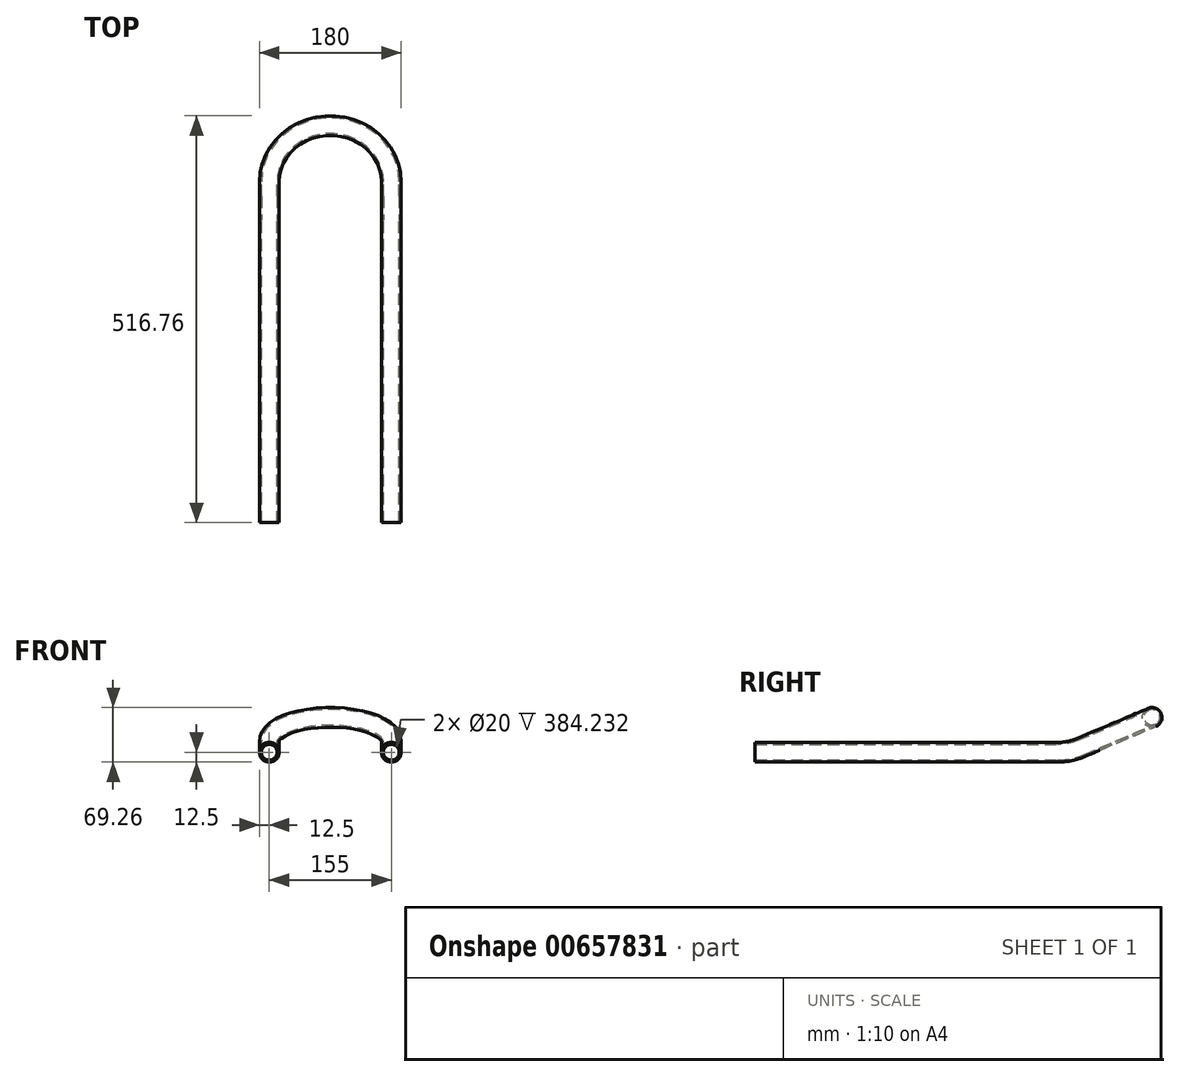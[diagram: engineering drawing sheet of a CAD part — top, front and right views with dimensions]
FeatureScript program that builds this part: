
annotation { "Feature Type Name" : "Feature", "Feature Type Description" : "" }
export const myFeature = defineFeature(function(context is Context, id is Id, definition is map)
    precondition{}
    {
        {
            var Q0;
            Q0=qCreatedBy(makeId("Top.planeOp"),FACE);
            var sketch = newSketch(context, id + "F0", { "sketchPlane" : qUnion([Q0])});
            skLineSegment(sketch, "E0", {"start": v(0, 0) * mm, "end": v(31.84, 0) * mm, "construction": true});
            skSolve(sketch);
        }
        {
            var Q0;
            Q0=qCreatedBy(makeId("Top.planeOp"),FACE);
            var Q1;
            Q1=sQuery(id+"F0.wireOp",EDGE,"E0");
            cPlane(context, id + "F1", {"entities" : qUnion([Q0, Q1]), "cplaneType" : CPlaneType.LINE_ANGLE, "offset" : 25.4 * mm, "angle" : 23 * degree, "width" : 152.4 * mm, "height" : 152.4 * mm});
        }
        {
            var Q0;
            Q0=qCreatedBy(makeId("Top.planeOp"),FACE);
            var sketch = newSketch(context, id + "F2", { "sketchPlane" : qUnion([Q0])});
            skLineSegment(sketch, "E1", {"start": v(77.5, 0) * mm, "end": v(77.5, -400) * mm});
            skSolve(sketch);
        }
        {
            var Q0;
            Q0=qCreatedBy(id+"F1.planeOp",FACE);
            var sketch = newSketch(context, id + "F3", { "sketchPlane" : qUnion([Q0])});
            skPoint(sketch, "E2.0", {"position": v(77.5, 0) * mm});
            skLineSegment(sketch, "E3", {"start": v(77.5, 0) * mm, "end": v(77.5, -35.77) * mm, "construction": true});
            skLineSegment(sketch, "E4", {"start": v(77.5, -35.77) * mm, "end": v(0, -35.77) * mm, "construction": true});
            skLineSegment(sketch, "E5", {"start": v(0, -35.77) * mm, "end": v(0, 0) * mm, "construction": true});
            skLineSegment(sketch, "E6", {"start": v(0, 0) * mm, "end": v(77.5, 0) * mm, "construction": true});
            skArc(sketch, "E7", {"start": v(77.5, -35.77) * mm, "mid": v(54.8, -90.57) * mm, "end": v(0, -113.27) * mm});
            skSolve(sketch);
        }
        {
            var Q0;
            Q0=sQuery(id+"F2.wireOp",VERTEX,"E1.end");
            var Q1;
            Q1=qCreatedBy(makeId("Front.planeOp"),FACE);
            cPlane(context, id + "F4", {"entities" : qUnion([Q0, Q1]), "cplaneType" : CPlaneType.PLANE_POINT, "offset" : 25 * mm, "width" : 150 * mm, "height" : 150 * mm});
        }
        {
            var Q0;
            Q0=qCreatedBy(id+"F4.planeOp",FACE);
            var sketch = newSketch(context, id + "F5", { "sketchPlane" : qUnion([Q0])});
            skPoint(sketch, "E8.0", {"position": v(77.5, 0) * mm});
            skCircle(sketch, "E9", {"center": v(77.5, 0) * mm, "radius": 12.5 * mm});
            skCircle(sketch, "E10.0", {"center": v(77.5, 0) * mm, "radius": 10 * mm});
            skSolve(sketch);
        }
        {
            var Q0;
            Q0=sQuery(id+"F2.wireOp",EDGE,"E1");
            var Q1;
            Q1=sQuery(id+"F3.wireOp",EDGE,"E3");
            cPlane(context, id + "F6", {"entities" : qUnion([Q0, Q1]), "cplaneType" : CPlaneType.LINE_ANGLE, "offset" : 25 * mm, "angle" : 0 * degree, "width" : 150 * mm, "height" : 150 * mm});
        }
        {
            var Q0;
            Q0=qCreatedBy(id+"F6.planeOp",FACE);
            var sketch = newSketch(context, id + "F7", { "sketchPlane" : qUnion([Q0])});
            skLineSegment(sketch, "E11.0", {"start": v(-14.51, 6.16) * mm, "end": v(-32.92, 13.98) * mm});
            skLineSegment(sketch, "E11.1", {"start": v(15.77, 0) * mm, "end": v(400, 0) * mm});
            skPoint(sketch, "E12.visualSharp", {"position": v(0, 0) * mm});
            skArc(sketch, "E12.filletArc", {"start": v(-14.51, 6.16) * mm, "mid": v(0.32, 1.56) * mm, "end": v(15.77, 0) * mm});
            skPoint(sketch, "E13", {"position": v(15.77, 0) * mm});
            skPoint(sketch, "E14", {"position": v(-14.51, 6.16) * mm});
            skSolve(sketch);
        }
        {
            var Q0;
            Q0=makeQuery(id+"F5.imprint","IMPRINT",FACE,{"disambiguationData":[TD([[makeQuery(id+"F5.imprint","IMPRINT",EDGE,{"derivedFrom":sQuery(id+"F5.wireOp",EDGE,"E9")}),1.0]])]});
            var Q1;
            Q1=sQuery(id+"F7.wireOp",EDGE,"E11.1");
            var Q2;
            Q2=sQuery(id+"F7.wireOp",EDGE,"E12.filletArc");
            var Q3;
            Q3=sQuery(id+"F7.wireOp",EDGE,"E11.0");
            var Q4;
            Q4=sQuery(id+"F3.wireOp",EDGE,"E7");
            sweep(context, id + "F8", {"profiles" : qUnion([Q0]), "path" : qUnion([Q1, Q2, Q3, Q4])});
        }
        {
            var Q0;
            Q0=makeQuery(id+"F8.opSweep","SWEPT_BODY",BODY,{"disambiguationData":[OSD([sQuery(id+"F3.wireOp",EDGE,"E7"),sQuery(id+"F5.wireOp",EDGE,"E9"),sQuery(id+"F5.wireOp",EDGE,"E10.0")])]});
            var Q1;
            Q1=qCreatedBy(makeId("Right.planeOp"),FACE);
            mirror(context, id + "F9", {"operationType" : NewBodyOperationType.ADD, "entities" : qUnion([Q0]), "mirrorPlane" : qUnion([Q1])});
        }
    });
